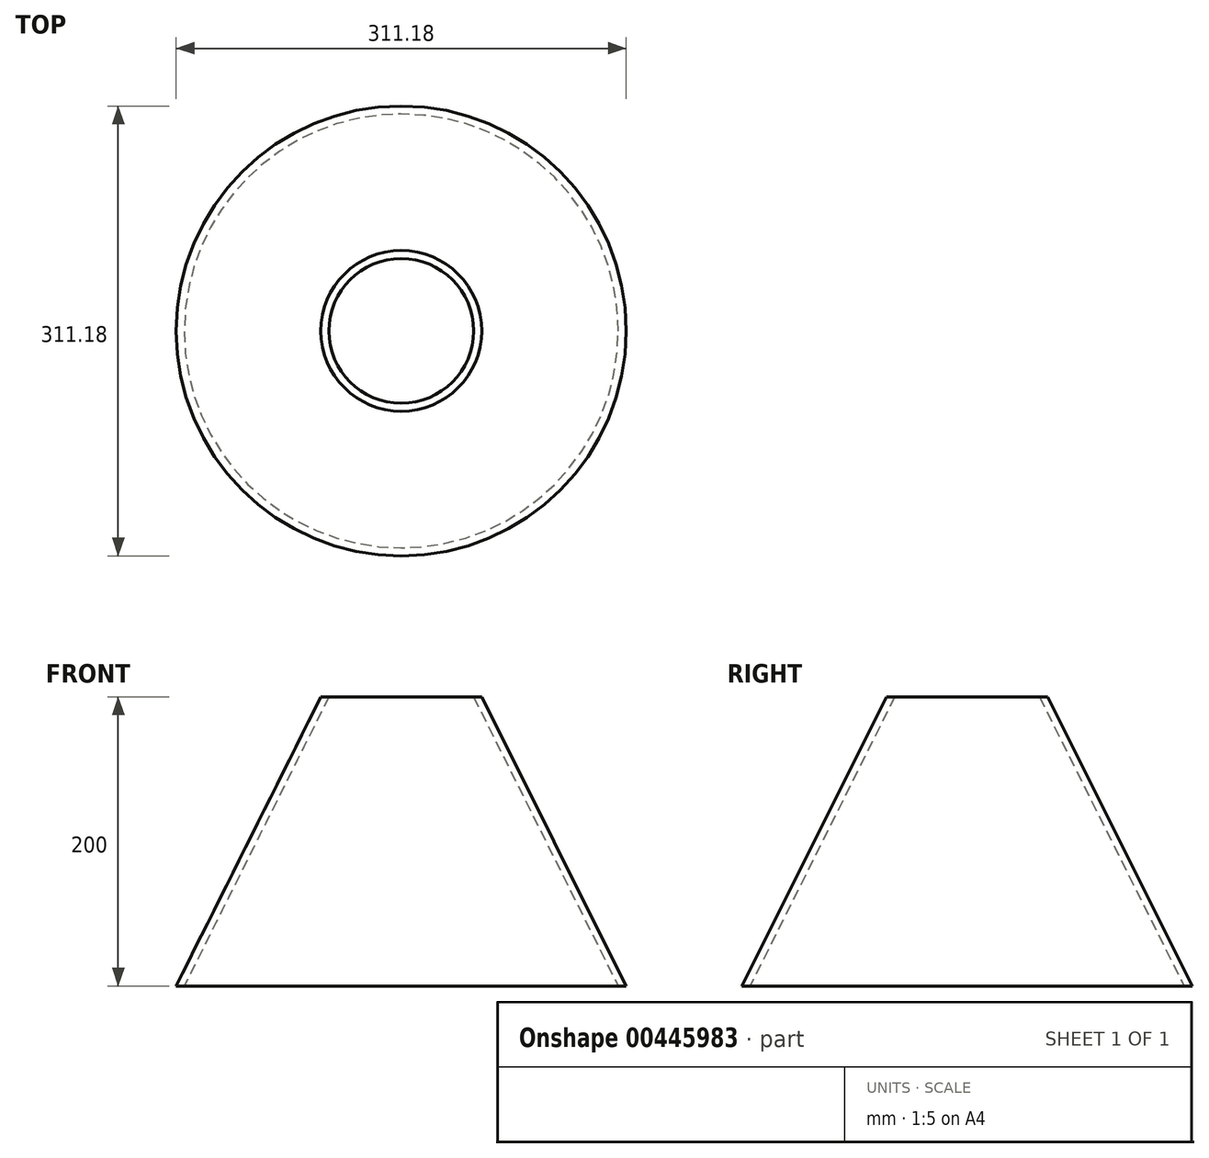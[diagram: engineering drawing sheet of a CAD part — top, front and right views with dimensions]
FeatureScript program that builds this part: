
annotation { "Feature Type Name" : "Feature", "Feature Type Description" : "" }
export const myFeature = defineFeature(function(context is Context, id is Id, definition is map)
    precondition{}
    {
        {
            var Q0;
            Q0=qCreatedBy(makeId("Front.planeOp"),FACE);
            var sketch = newSketch(context, id + "F0", { "sketchPlane" : qUnion([Q0])});
            skLineSegment(sketch, "E0", {"start": v(0, 0) * mm, "end": v(0, 200) * mm});
            skLineSegment(sketch, "E1", {"start": v(0, 200) * mm, "end": v(-50, 200) * mm});
            skLineSegment(sketch, "E2", {"start": v(-50, 200) * mm, "end": v(-150, 0) * mm});
            skLineSegment(sketch, "E3", {"start": v(-150, 0) * mm, "end": v(0, 0) * mm});
            skSolve(sketch);
        }
        {
            var Q0;
            Q0=makeQuery(id+"F0.imprint","IMPRINT",FACE,{"disambiguationData":[TD([[makeQuery(id+"F0.imprint","IMPRINT",EDGE,{"derivedFrom":sQuery(id+"F0.wireOp",EDGE,"E0")}),1.0]])]});
            var Q1;
            Q1=sQuery(id+"F0.wireOp",EDGE,"E0");
            revolve(context, id + "F1", {"entities" : qUnion([Q0]), "axis" : qUnion([Q1]), "revolveType" : RevolveType.FULL});
        }
        {
            var Q0;
            Q0=makeQuery(id+"F1.opRevolve","SWEPT_FACE",FACE,{"disambiguationData":[OSD([sQuery(id+"F0.wireOp",EDGE,"E1")])]});
            var Q1;
            Q1=makeQuery(id+"F1.opRevolve","SWEPT_FACE",FACE,{"disambiguationData":[OSD([sQuery(id+"F0.wireOp",EDGE,"E3")])]});
            shell(context, id + "F2", {"entities" : qUnion([Q0, Q1]), "thickness" : 5 * mm, "oppositeDirection" : true});
        }
    });
